# Revit family: Kabelrinne SKS-SKS 640_FT_FS_FTK_FTSO_FTKK_A2_A4
name_source: partatom
category: Generic Models
revit_build: Autodesk Revit 2017 (Build: 20190508_0315(x64)
units: mm (PartAtom-declared; Revit-internal decimal feet)

## family parameters
Always vertical = Yes
Can host rebar = No
Cut with Voids When Loaded = No
Part Type = Normal
Room Calculation Point = No
Round Connector Dimension = Use Diameter
Shared = No
Work Plane-Based = No

## types (6) — shared parameters
Cut's number = 2
Cut's number 2 = 60
Cut's number 3 = 59
Cut's space = 50 mm  [stored 0.164042 ft]
Height = 51 mm
Length = 3000 mm  [stored 9.84252 ft]
Manufacturer = OBO BETTERMANN
URL = http:/www.obo-bettermann.com
Width = 400 mm  [stored 1.31234 ft]
Width 1 = 200 mm  [stored 0.656168 ft]

## per-type parameters (varying)
| type | GTIN | Manufacturer Art.No. | Material |
| SKS 640 FT | 4012196060559 | 6056695 | Strip-galvanised |
| SKS 640 A2 | 4012196120734 | 6056742 | hot-dip galvanised |
| SKS 640 A4 | 4012196050284 | 6056759 | Edelstahl, rostfrei A4 |
| SKS 640 FS | 4012196060375 | 6056407 | hot-dip galvanised |
| SKS 640 FT SO | 4012196014897 | 7190158 | Hot dip galvanised |
| SKS 640 FTK LGR | 4012196623532 | 6056409 | Polyester/Epoxid/Korrosionschutz |

note: column(s) folded — value = type name in every type: Article Type

note: [stored X ft] marks values corroborated as IEEE doubles in the binary element streams (Revit-internal decimal feet)

## geometry (parser evidence)
native form markers: Sweep x2
no freeform markers — native parametric forms only
